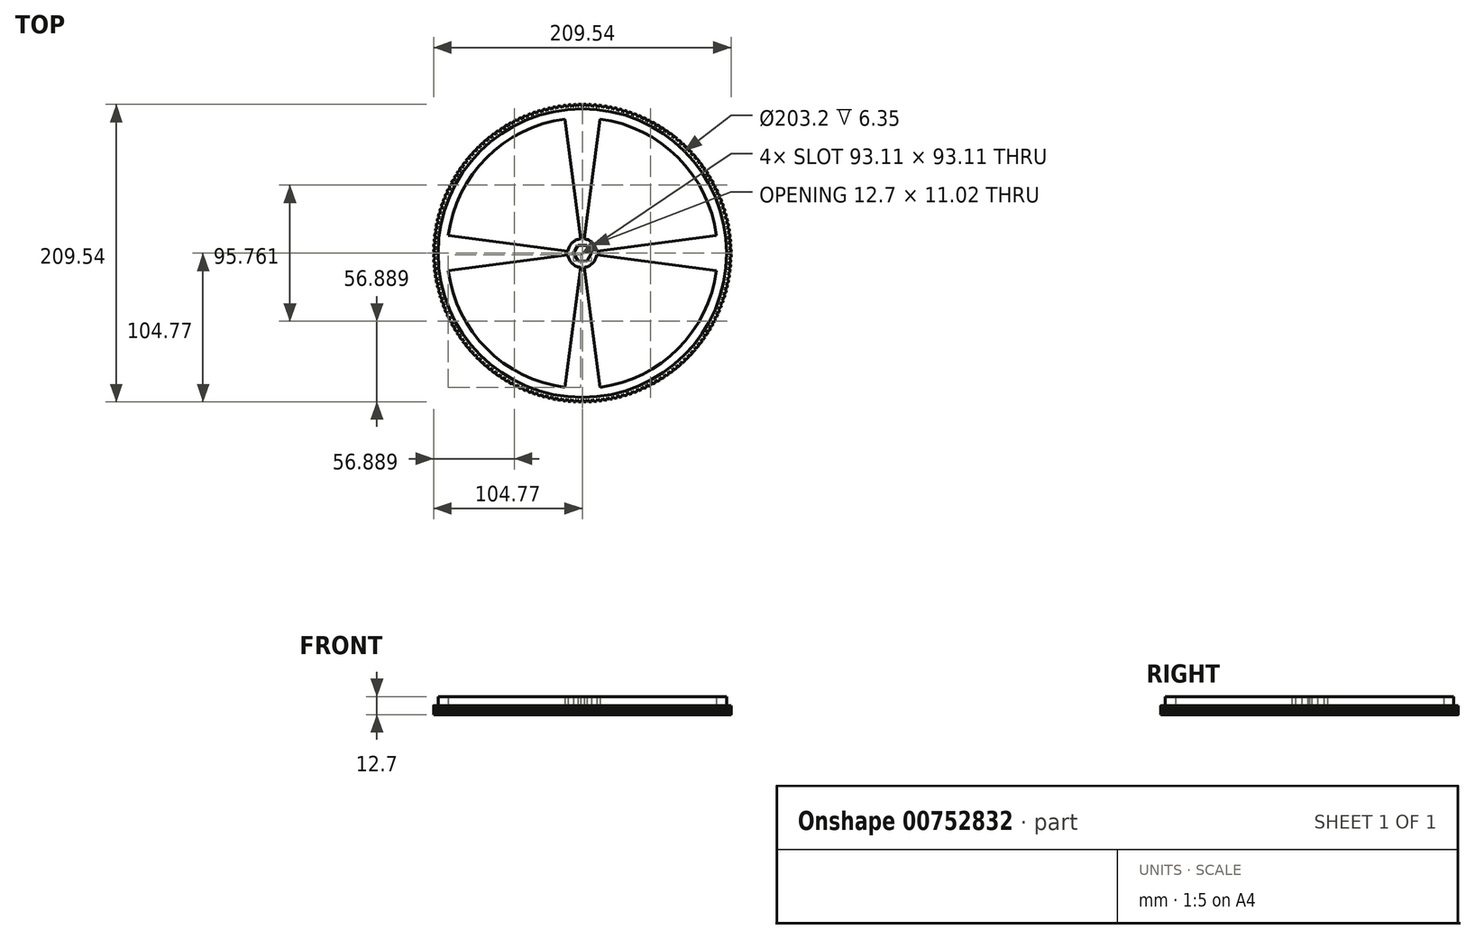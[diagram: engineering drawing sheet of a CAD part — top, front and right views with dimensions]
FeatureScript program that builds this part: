
annotation { "Feature Type Name" : "Feature", "Feature Type Description" : "" }
export const myFeature = defineFeature(function(context is Context, id is Id, definition is map)
    precondition{}
    {
        {
            var Q0;
            Q0=qCreatedBy(makeId("Top.planeOp"),FACE);
            var sketch = newSketch(context, id + "F0", { "sketchPlane" : qUnion([Q0])});
            skLineSegment(sketch, "E0.0", {"start": v(-3.15, 5.51) * mm, "end": v(3.2, 5.49) * mm});
            skLineSegment(sketch, "E0.1", {"start": v(3.2, 5.49) * mm, "end": v(6.35, -0.03) * mm});
            skLineSegment(sketch, "E0.2", {"start": v(6.35, -0.03) * mm, "end": v(3.15, -5.51) * mm});
            skLineSegment(sketch, "E0.3", {"start": v(3.15, -5.51) * mm, "end": v(-3.2, -5.49) * mm});
            skLineSegment(sketch, "E0.4", {"start": v(-3.2, -5.49) * mm, "end": v(-6.35, 0.03) * mm});
            skLineSegment(sketch, "E0.5", {"start": v(-6.35, 0.03) * mm, "end": v(-3.15, 5.51) * mm});
            skArc(sketch, "E1", {"start": v(-10.07, -1.33) * mm, "mid": v(-7.18, -7.18) * mm, "end": v(-1.33, -10.07) * mm});
            skCircle(sketch, "E2", {"center": v(0, 0) * mm, "radius": 101.6 * mm});
            skArc(sketch, "E3", {"start": v(94.44, 12.43) * mm, "mid": v(67.35, 67.35) * mm, "end": v(12.43, 94.44) * mm});
            skLineSegment(sketch, "E4", {"start": v(1.33, 10.07) * mm, "end": v(12.43, 94.44) * mm});
            skLineSegment(sketch, "E5", {"start": v(-1.33, 10.07) * mm, "end": v(-12.43, 94.44) * mm});
            skLineSegment(sketch, "E6.trimOffspring", {"start": v(-10.07, 1.33) * mm, "end": v(-94.44, 12.43) * mm});
            skLineSegment(sketch, "E7.trimOffspring", {"start": v(-10.07, -1.33) * mm, "end": v(-94.44, -12.43) * mm});
            skLineSegment(sketch, "E8.trimOffspring", {"start": v(-1.33, -10.07) * mm, "end": v(-12.43, -94.44) * mm});
            skLineSegment(sketch, "E9.trimOffspring", {"start": v(1.33, -10.07) * mm, "end": v(12.43, -94.44) * mm});
            skLineSegment(sketch, "E10.trimOffspring", {"start": v(10.07, -1.33) * mm, "end": v(94.44, -12.43) * mm});
            skLineSegment(sketch, "E11.trimOffspring", {"start": v(10.07, 1.33) * mm, "end": v(94.44, 12.43) * mm});
            skArc(sketch, "E12.trimOffspring", {"start": v(-12.43, 94.44) * mm, "mid": v(-67.35, 67.35) * mm, "end": v(-94.44, 12.43) * mm});
            skArc(sketch, "E13.trimOffspring", {"start": v(-94.44, -12.43) * mm, "mid": v(-67.35, -67.35) * mm, "end": v(-12.43, -94.44) * mm});
            skArc(sketch, "E14.trimOffspring", {"start": v(12.43, -94.44) * mm, "mid": v(67.35, -67.35) * mm, "end": v(94.44, -12.43) * mm});
            skArc(sketch, "E15.trimOffspring", {"start": v(-1.33, 10.07) * mm, "mid": v(-7.18, 7.18) * mm, "end": v(-10.07, 1.33) * mm});
            skArc(sketch, "E16.trimOffspring", {"start": v(10.07, 1.33) * mm, "mid": v(7.18, 7.18) * mm, "end": v(1.33, 10.07) * mm});
            skArc(sketch, "E17.trimOffspring", {"start": v(1.33, -10.07) * mm, "mid": v(7.18, -7.18) * mm, "end": v(10.07, -1.33) * mm});
            skSolve(sketch);
        }
        {
            var Q0;
            Q0 = qSketchRegion(id + "F0", true);
            extrude(context, id + "F1", {"entities" : qUnion([Q0]), "depth" : 6.35 * mm, "offsetDistance" : 25.4 * mm});
        }
        {
            var Q0;
            Q0=qCreatedBy(makeId("Top.planeOp"),FACE);
            var sketch = newSketch(context, id + "F2", { "sketchPlane" : qUnion([Q0])});
            skCircle(sketch, "E18", {"center": v(0, 0) * mm, "radius": 101.6 * mm});
            skCircle(sketch, "E19", {"center": v(0, 0) * mm, "radius": 104.78 * mm});
            skLineSegment(sketch, "E20", {"start": v(0, -103.19) * mm, "end": v(-0.91, -104.77) * mm});
            skLineSegment(sketch, "E21", {"start": v(0, -103.19) * mm, "end": v(0.91, -104.77) * mm});
            skLineSegment(sketch, "E22.1.0", {"start": v(3.6, -103.12) * mm, "end": v(4.57, -104.68) * mm});
            skLineSegment(sketch, "E22.1.1", {"start": v(3.6, -103.12) * mm, "end": v(2.74, -104.74) * mm});
            skLineSegment(sketch, "E22.2.0", {"start": v(7.2, -102.94) * mm, "end": v(8.22, -104.45) * mm});
            skLineSegment(sketch, "E22.2.1", {"start": v(7.2, -102.94) * mm, "end": v(6.4, -104.58) * mm});
            skLineSegment(sketch, "E22.3.0", {"start": v(10.79, -102.62) * mm, "end": v(11.86, -104.1) * mm});
            skLineSegment(sketch, "E22.3.1", {"start": v(10.79, -102.62) * mm, "end": v(10.04, -104.3) * mm});
            skLineSegment(sketch, "E22.4.0", {"start": v(14.36, -102.18) * mm, "end": v(15.49, -103.62) * mm});
            skLineSegment(sketch, "E22.4.1", {"start": v(14.36, -102.18) * mm, "end": v(13.68, -103.88) * mm});
            skLineSegment(sketch, "E22.5.0", {"start": v(17.92, -101.62) * mm, "end": v(19.1, -103.02) * mm});
            skLineSegment(sketch, "E22.5.1", {"start": v(17.92, -101.62) * mm, "end": v(17.3, -103.34) * mm});
            skLineSegment(sketch, "E22.6.0", {"start": v(21.45, -100.93) * mm, "end": v(22.68, -102.3) * mm});
            skLineSegment(sketch, "E22.6.1", {"start": v(21.45, -100.93) * mm, "end": v(20.89, -102.67) * mm});
            skLineSegment(sketch, "E22.7.0", {"start": v(24.96, -100.12) * mm, "end": v(26.23, -101.44) * mm});
            skLineSegment(sketch, "E22.7.1", {"start": v(24.96, -100.12) * mm, "end": v(24.46, -101.88) * mm});
            skLineSegment(sketch, "E22.8.0", {"start": v(28.44, -99.2) * mm, "end": v(29.76, -100.46) * mm});
            skLineSegment(sketch, "E22.8.1", {"start": v(28.44, -99.2) * mm, "end": v(28, -100.96) * mm});
            skLineSegment(sketch, "E22.9.0", {"start": v(31.89, -98.14) * mm, "end": v(33.25, -99.36) * mm});
            skLineSegment(sketch, "E22.9.1", {"start": v(31.89, -98.14) * mm, "end": v(31.5, -99.93) * mm});
            skLineSegment(sketch, "E22.10.0", {"start": v(35.3, -96.96) * mm, "end": v(36.7, -98.14) * mm});
            skLineSegment(sketch, "E22.10.1", {"start": v(35.3, -96.96) * mm, "end": v(34.97, -98.77) * mm});
            skLineSegment(sketch, "E22.11.0", {"start": v(38.65, -95.67) * mm, "end": v(40.1, -96.8) * mm});
            skLineSegment(sketch, "E22.11.1", {"start": v(38.65, -95.67) * mm, "end": v(38.4, -97.48) * mm});
            skLineSegment(sketch, "E22.12.0", {"start": v(41.97, -94.27) * mm, "end": v(43.45, -95.34) * mm});
            skLineSegment(sketch, "E22.12.1", {"start": v(41.97, -94.27) * mm, "end": v(41.78, -96.08) * mm});
            skLineSegment(sketch, "E22.13.0", {"start": v(45.23, -92.74) * mm, "end": v(46.75, -93.77) * mm});
            skLineSegment(sketch, "E22.13.1", {"start": v(45.23, -92.74) * mm, "end": v(45.1, -94.57) * mm});
            skLineSegment(sketch, "E22.14.0", {"start": v(48.44, -91.1) * mm, "end": v(50, -92.08) * mm});
            skLineSegment(sketch, "E22.14.1", {"start": v(48.44, -91.1) * mm, "end": v(48.38, -92.94) * mm});
            skLineSegment(sketch, "E22.15.0", {"start": v(51.6, -89.36) * mm, "end": v(53.18, -90.28) * mm});
            skLineSegment(sketch, "E22.15.1", {"start": v(51.6, -89.36) * mm, "end": v(51.6, -91.2) * mm});
            skLineSegment(sketch, "E22.16.0", {"start": v(54.68, -87.5) * mm, "end": v(56.3, -88.37) * mm});
            skLineSegment(sketch, "E22.16.1", {"start": v(54.68, -87.5) * mm, "end": v(54.74, -89.34) * mm});
            skLineSegment(sketch, "E22.17.0", {"start": v(57.7, -85.55) * mm, "end": v(59.35, -86.35) * mm});
            skLineSegment(sketch, "E22.17.1", {"start": v(57.7, -85.55) * mm, "end": v(57.83, -87.37) * mm});
            skLineSegment(sketch, "E22.18.0", {"start": v(60.65, -83.48) * mm, "end": v(62.32, -84.22) * mm});
            skLineSegment(sketch, "E22.18.1", {"start": v(60.65, -83.48) * mm, "end": v(60.84, -85.3) * mm});
            skLineSegment(sketch, "E22.19.0", {"start": v(63.53, -81.31) * mm, "end": v(65.22, -82) * mm});
            skLineSegment(sketch, "E22.19.1", {"start": v(63.53, -81.31) * mm, "end": v(63.78, -83.12) * mm});
            skLineSegment(sketch, "E22.20.0", {"start": v(66.33, -79.05) * mm, "end": v(68.05, -79.67) * mm});
            skLineSegment(sketch, "E22.20.1", {"start": v(66.33, -79.05) * mm, "end": v(66.65, -80.85) * mm});
            skLineSegment(sketch, "E22.21.0", {"start": v(69.05, -76.68) * mm, "end": v(70.78, -77.25) * mm});
            skLineSegment(sketch, "E22.21.1", {"start": v(69.05, -76.68) * mm, "end": v(69.43, -78.47) * mm});
            skLineSegment(sketch, "E22.22.0", {"start": v(71.68, -74.23) * mm, "end": v(73.44, -74.73) * mm});
            skLineSegment(sketch, "E22.22.1", {"start": v(71.68, -74.23) * mm, "end": v(72.12, -76) * mm});
            skLineSegment(sketch, "E22.23.0", {"start": v(74.23, -71.68) * mm, "end": v(76, -72.12) * mm});
            skLineSegment(sketch, "E22.23.1", {"start": v(74.23, -71.68) * mm, "end": v(74.73, -73.44) * mm});
            skLineSegment(sketch, "E22.24.0", {"start": v(76.68, -69.05) * mm, "end": v(78.47, -69.43) * mm});
            skLineSegment(sketch, "E22.24.1", {"start": v(76.68, -69.05) * mm, "end": v(77.25, -70.78) * mm});
            skLineSegment(sketch, "E22.25.0", {"start": v(79.05, -66.33) * mm, "end": v(80.85, -66.65) * mm});
            skLineSegment(sketch, "E22.25.1", {"start": v(79.05, -66.33) * mm, "end": v(79.67, -68.05) * mm});
            skLineSegment(sketch, "E22.26.0", {"start": v(81.31, -63.53) * mm, "end": v(83.12, -63.78) * mm});
            skLineSegment(sketch, "E22.26.1", {"start": v(81.31, -63.53) * mm, "end": v(82, -65.22) * mm});
            skLineSegment(sketch, "E22.27.0", {"start": v(83.48, -60.65) * mm, "end": v(85.3, -60.84) * mm});
            skLineSegment(sketch, "E22.27.1", {"start": v(83.48, -60.65) * mm, "end": v(84.22, -62.32) * mm});
            skLineSegment(sketch, "E22.28.0", {"start": v(85.55, -57.7) * mm, "end": v(87.37, -57.83) * mm});
            skLineSegment(sketch, "E22.28.1", {"start": v(85.55, -57.7) * mm, "end": v(86.35, -59.35) * mm});
            skLineSegment(sketch, "E22.29.0", {"start": v(87.5, -54.68) * mm, "end": v(89.34, -54.74) * mm});
            skLineSegment(sketch, "E22.29.1", {"start": v(87.5, -54.68) * mm, "end": v(88.37, -56.3) * mm});
            skLineSegment(sketch, "E22.30.0", {"start": v(89.36, -51.6) * mm, "end": v(91.2, -51.6) * mm});
            skLineSegment(sketch, "E22.30.1", {"start": v(89.36, -51.6) * mm, "end": v(90.28, -53.18) * mm});
            skLineSegment(sketch, "E22.31.0", {"start": v(91.1, -48.44) * mm, "end": v(92.94, -48.38) * mm});
            skLineSegment(sketch, "E22.31.1", {"start": v(91.1, -48.44) * mm, "end": v(92.08, -50) * mm});
            skLineSegment(sketch, "E22.32.0", {"start": v(92.74, -45.23) * mm, "end": v(94.57, -45.1) * mm});
            skLineSegment(sketch, "E22.32.1", {"start": v(92.74, -45.23) * mm, "end": v(93.77, -46.75) * mm});
            skLineSegment(sketch, "E22.33.0", {"start": v(94.27, -41.97) * mm, "end": v(96.08, -41.78) * mm});
            skLineSegment(sketch, "E22.33.1", {"start": v(94.27, -41.97) * mm, "end": v(95.34, -43.45) * mm});
            skLineSegment(sketch, "E22.34.0", {"start": v(95.67, -38.65) * mm, "end": v(97.48, -38.4) * mm});
            skLineSegment(sketch, "E22.34.1", {"start": v(95.67, -38.65) * mm, "end": v(96.8, -40.1) * mm});
            skLineSegment(sketch, "E22.35.0", {"start": v(96.96, -35.3) * mm, "end": v(98.77, -34.97) * mm});
            skLineSegment(sketch, "E22.35.1", {"start": v(96.96, -35.3) * mm, "end": v(98.14, -36.7) * mm});
            skLineSegment(sketch, "E22.36.0", {"start": v(98.14, -31.89) * mm, "end": v(99.93, -31.5) * mm});
            skLineSegment(sketch, "E22.36.1", {"start": v(98.14, -31.89) * mm, "end": v(99.36, -33.25) * mm});
            skLineSegment(sketch, "E22.37.0", {"start": v(99.2, -28.44) * mm, "end": v(100.96, -28) * mm});
            skLineSegment(sketch, "E22.37.1", {"start": v(99.2, -28.44) * mm, "end": v(100.46, -29.76) * mm});
            skLineSegment(sketch, "E22.38.0", {"start": v(100.12, -24.96) * mm, "end": v(101.88, -24.46) * mm});
            skLineSegment(sketch, "E22.38.1", {"start": v(100.12, -24.96) * mm, "end": v(101.44, -26.23) * mm});
            skLineSegment(sketch, "E22.39.0", {"start": v(100.93, -21.45) * mm, "end": v(102.67, -20.89) * mm});
            skLineSegment(sketch, "E22.39.1", {"start": v(100.93, -21.45) * mm, "end": v(102.3, -22.68) * mm});
            skLineSegment(sketch, "E22.40.0", {"start": v(101.62, -17.92) * mm, "end": v(103.34, -17.3) * mm});
            skLineSegment(sketch, "E22.40.1", {"start": v(101.62, -17.92) * mm, "end": v(103.02, -19.1) * mm});
            skLineSegment(sketch, "E22.41.0", {"start": v(102.18, -14.36) * mm, "end": v(103.88, -13.68) * mm});
            skLineSegment(sketch, "E22.41.1", {"start": v(102.18, -14.36) * mm, "end": v(103.62, -15.49) * mm});
            skLineSegment(sketch, "E22.42.0", {"start": v(102.62, -10.79) * mm, "end": v(104.3, -10.04) * mm});
            skLineSegment(sketch, "E22.42.1", {"start": v(102.62, -10.79) * mm, "end": v(104.1, -11.86) * mm});
            skLineSegment(sketch, "E22.43.0", {"start": v(102.94, -7.2) * mm, "end": v(104.58, -6.4) * mm});
            skLineSegment(sketch, "E22.43.1", {"start": v(102.94, -7.2) * mm, "end": v(104.45, -8.22) * mm});
            skLineSegment(sketch, "E22.44.0", {"start": v(103.12, -3.6) * mm, "end": v(104.74, -2.74) * mm});
            skLineSegment(sketch, "E22.44.1", {"start": v(103.12, -3.6) * mm, "end": v(104.68, -4.57) * mm});
            skLineSegment(sketch, "E22.45.0", {"start": v(103.19, 0) * mm, "end": v(104.77, 0.91) * mm});
            skLineSegment(sketch, "E22.45.1", {"start": v(103.19, 0) * mm, "end": v(104.77, -0.91) * mm});
            skLineSegment(sketch, "E22.46.0", {"start": v(103.12, 3.6) * mm, "end": v(104.68, 4.57) * mm});
            skLineSegment(sketch, "E22.46.1", {"start": v(103.12, 3.6) * mm, "end": v(104.74, 2.74) * mm});
            skLineSegment(sketch, "E22.47.0", {"start": v(102.94, 7.2) * mm, "end": v(104.45, 8.22) * mm});
            skLineSegment(sketch, "E22.47.1", {"start": v(102.94, 7.2) * mm, "end": v(104.58, 6.4) * mm});
            skLineSegment(sketch, "E22.48.0", {"start": v(102.62, 10.79) * mm, "end": v(104.1, 11.86) * mm});
            skLineSegment(sketch, "E22.48.1", {"start": v(102.62, 10.79) * mm, "end": v(104.3, 10.04) * mm});
            skLineSegment(sketch, "E22.49.0", {"start": v(102.18, 14.36) * mm, "end": v(103.62, 15.49) * mm});
            skLineSegment(sketch, "E22.49.1", {"start": v(102.18, 14.36) * mm, "end": v(103.88, 13.68) * mm});
            skLineSegment(sketch, "E22.50.0", {"start": v(101.62, 17.92) * mm, "end": v(103.02, 19.1) * mm});
            skLineSegment(sketch, "E22.50.1", {"start": v(101.62, 17.92) * mm, "end": v(103.34, 17.3) * mm});
            skLineSegment(sketch, "E22.51.0", {"start": v(100.93, 21.45) * mm, "end": v(102.3, 22.68) * mm});
            skLineSegment(sketch, "E22.51.1", {"start": v(100.93, 21.45) * mm, "end": v(102.67, 20.89) * mm});
            skLineSegment(sketch, "E22.52.0", {"start": v(100.12, 24.96) * mm, "end": v(101.44, 26.23) * mm});
            skLineSegment(sketch, "E22.52.1", {"start": v(100.12, 24.96) * mm, "end": v(101.88, 24.46) * mm});
            skLineSegment(sketch, "E22.53.0", {"start": v(99.2, 28.44) * mm, "end": v(100.46, 29.76) * mm});
            skLineSegment(sketch, "E22.53.1", {"start": v(99.2, 28.44) * mm, "end": v(100.96, 28) * mm});
            skLineSegment(sketch, "E22.54.0", {"start": v(98.14, 31.89) * mm, "end": v(99.36, 33.25) * mm});
            skLineSegment(sketch, "E22.54.1", {"start": v(98.14, 31.89) * mm, "end": v(99.93, 31.5) * mm});
            skLineSegment(sketch, "E22.55.0", {"start": v(96.96, 35.3) * mm, "end": v(98.14, 36.7) * mm});
            skLineSegment(sketch, "E22.55.1", {"start": v(96.96, 35.3) * mm, "end": v(98.77, 34.97) * mm});
            skLineSegment(sketch, "E22.56.0", {"start": v(95.67, 38.65) * mm, "end": v(96.8, 40.1) * mm});
            skLineSegment(sketch, "E22.56.1", {"start": v(95.67, 38.65) * mm, "end": v(97.48, 38.4) * mm});
            skLineSegment(sketch, "E22.57.0", {"start": v(94.27, 41.97) * mm, "end": v(95.34, 43.45) * mm});
            skLineSegment(sketch, "E22.57.1", {"start": v(94.27, 41.97) * mm, "end": v(96.08, 41.78) * mm});
            skLineSegment(sketch, "E22.58.0", {"start": v(92.74, 45.23) * mm, "end": v(93.77, 46.75) * mm});
            skLineSegment(sketch, "E22.58.1", {"start": v(92.74, 45.23) * mm, "end": v(94.57, 45.1) * mm});
            skLineSegment(sketch, "E22.59.0", {"start": v(91.1, 48.44) * mm, "end": v(92.08, 50) * mm});
            skLineSegment(sketch, "E22.59.1", {"start": v(91.1, 48.44) * mm, "end": v(92.94, 48.38) * mm});
            skLineSegment(sketch, "E22.60.0", {"start": v(89.36, 51.6) * mm, "end": v(90.28, 53.18) * mm});
            skLineSegment(sketch, "E22.60.1", {"start": v(89.36, 51.6) * mm, "end": v(91.2, 51.6) * mm});
            skLineSegment(sketch, "E22.61.0", {"start": v(87.5, 54.68) * mm, "end": v(88.37, 56.3) * mm});
            skLineSegment(sketch, "E22.61.1", {"start": v(87.5, 54.68) * mm, "end": v(89.34, 54.74) * mm});
            skLineSegment(sketch, "E22.62.0", {"start": v(85.55, 57.7) * mm, "end": v(86.35, 59.35) * mm});
            skLineSegment(sketch, "E22.62.1", {"start": v(85.55, 57.7) * mm, "end": v(87.37, 57.83) * mm});
            skLineSegment(sketch, "E22.63.0", {"start": v(83.48, 60.65) * mm, "end": v(84.22, 62.32) * mm});
            skLineSegment(sketch, "E22.63.1", {"start": v(83.48, 60.65) * mm, "end": v(85.3, 60.84) * mm});
            skLineSegment(sketch, "E22.64.0", {"start": v(81.31, 63.53) * mm, "end": v(82, 65.22) * mm});
            skLineSegment(sketch, "E22.64.1", {"start": v(81.31, 63.53) * mm, "end": v(83.12, 63.78) * mm});
            skLineSegment(sketch, "E22.65.0", {"start": v(79.05, 66.33) * mm, "end": v(79.67, 68.05) * mm});
            skLineSegment(sketch, "E22.65.1", {"start": v(79.05, 66.33) * mm, "end": v(80.85, 66.65) * mm});
            skLineSegment(sketch, "E22.66.0", {"start": v(76.68, 69.05) * mm, "end": v(77.25, 70.78) * mm});
            skLineSegment(sketch, "E22.66.1", {"start": v(76.68, 69.05) * mm, "end": v(78.47, 69.43) * mm});
            skLineSegment(sketch, "E22.67.0", {"start": v(74.23, 71.68) * mm, "end": v(74.73, 73.44) * mm});
            skLineSegment(sketch, "E22.67.1", {"start": v(74.23, 71.68) * mm, "end": v(76, 72.12) * mm});
            skLineSegment(sketch, "E22.68.0", {"start": v(71.68, 74.23) * mm, "end": v(72.12, 76) * mm});
            skLineSegment(sketch, "E22.68.1", {"start": v(71.68, 74.23) * mm, "end": v(73.44, 74.73) * mm});
            skLineSegment(sketch, "E22.69.0", {"start": v(69.05, 76.68) * mm, "end": v(69.43, 78.47) * mm});
            skLineSegment(sketch, "E22.69.1", {"start": v(69.05, 76.68) * mm, "end": v(70.78, 77.25) * mm});
            skLineSegment(sketch, "E22.70.0", {"start": v(66.33, 79.05) * mm, "end": v(66.65, 80.85) * mm});
            skLineSegment(sketch, "E22.70.1", {"start": v(66.33, 79.05) * mm, "end": v(68.05, 79.67) * mm});
            skLineSegment(sketch, "E22.71.0", {"start": v(63.53, 81.31) * mm, "end": v(63.78, 83.12) * mm});
            skLineSegment(sketch, "E22.71.1", {"start": v(63.53, 81.31) * mm, "end": v(65.22, 82) * mm});
            skLineSegment(sketch, "E22.72.0", {"start": v(60.65, 83.48) * mm, "end": v(60.84, 85.3) * mm});
            skLineSegment(sketch, "E22.72.1", {"start": v(60.65, 83.48) * mm, "end": v(62.32, 84.22) * mm});
            skLineSegment(sketch, "E22.73.0", {"start": v(57.7, 85.55) * mm, "end": v(57.83, 87.37) * mm});
            skLineSegment(sketch, "E22.73.1", {"start": v(57.7, 85.55) * mm, "end": v(59.35, 86.35) * mm});
            skLineSegment(sketch, "E22.74.0", {"start": v(54.68, 87.5) * mm, "end": v(54.74, 89.34) * mm});
            skLineSegment(sketch, "E22.74.1", {"start": v(54.68, 87.5) * mm, "end": v(56.3, 88.37) * mm});
            skLineSegment(sketch, "E22.75.0", {"start": v(51.6, 89.36) * mm, "end": v(51.6, 91.2) * mm});
            skLineSegment(sketch, "E22.75.1", {"start": v(51.6, 89.36) * mm, "end": v(53.18, 90.28) * mm});
            skLineSegment(sketch, "E22.76.0", {"start": v(48.44, 91.1) * mm, "end": v(48.38, 92.94) * mm});
            skLineSegment(sketch, "E22.76.1", {"start": v(48.44, 91.1) * mm, "end": v(50, 92.08) * mm});
            skLineSegment(sketch, "E22.77.0", {"start": v(45.23, 92.74) * mm, "end": v(45.1, 94.57) * mm});
            skLineSegment(sketch, "E22.77.1", {"start": v(45.23, 92.74) * mm, "end": v(46.75, 93.77) * mm});
            skLineSegment(sketch, "E22.78.0", {"start": v(41.97, 94.27) * mm, "end": v(41.78, 96.08) * mm});
            skLineSegment(sketch, "E22.78.1", {"start": v(41.97, 94.27) * mm, "end": v(43.45, 95.34) * mm});
            skLineSegment(sketch, "E22.79.0", {"start": v(38.65, 95.67) * mm, "end": v(38.4, 97.48) * mm});
            skLineSegment(sketch, "E22.79.1", {"start": v(38.65, 95.67) * mm, "end": v(40.1, 96.8) * mm});
            skLineSegment(sketch, "E22.80.0", {"start": v(35.3, 96.96) * mm, "end": v(34.97, 98.77) * mm});
            skLineSegment(sketch, "E22.80.1", {"start": v(35.3, 96.96) * mm, "end": v(36.7, 98.14) * mm});
            skLineSegment(sketch, "E22.81.0", {"start": v(31.89, 98.14) * mm, "end": v(31.5, 99.93) * mm});
            skLineSegment(sketch, "E22.81.1", {"start": v(31.89, 98.14) * mm, "end": v(33.25, 99.36) * mm});
            skLineSegment(sketch, "E22.82.0", {"start": v(28.44, 99.2) * mm, "end": v(28, 100.96) * mm});
            skLineSegment(sketch, "E22.82.1", {"start": v(28.44, 99.2) * mm, "end": v(29.76, 100.46) * mm});
            skLineSegment(sketch, "E22.83.0", {"start": v(24.96, 100.12) * mm, "end": v(24.46, 101.88) * mm});
            skLineSegment(sketch, "E22.83.1", {"start": v(24.96, 100.12) * mm, "end": v(26.23, 101.44) * mm});
            skLineSegment(sketch, "E22.84.0", {"start": v(21.45, 100.93) * mm, "end": v(20.89, 102.67) * mm});
            skLineSegment(sketch, "E22.84.1", {"start": v(21.45, 100.93) * mm, "end": v(22.68, 102.3) * mm});
            skLineSegment(sketch, "E22.85.0", {"start": v(17.92, 101.62) * mm, "end": v(17.3, 103.34) * mm});
            skLineSegment(sketch, "E22.85.1", {"start": v(17.92, 101.62) * mm, "end": v(19.1, 103.02) * mm});
            skLineSegment(sketch, "E22.86.0", {"start": v(14.36, 102.18) * mm, "end": v(13.68, 103.88) * mm});
            skLineSegment(sketch, "E22.86.1", {"start": v(14.36, 102.18) * mm, "end": v(15.49, 103.62) * mm});
            skLineSegment(sketch, "E22.87.0", {"start": v(10.79, 102.62) * mm, "end": v(10.04, 104.3) * mm});
            skLineSegment(sketch, "E22.87.1", {"start": v(10.79, 102.62) * mm, "end": v(11.86, 104.1) * mm});
            skLineSegment(sketch, "E22.88.0", {"start": v(7.2, 102.94) * mm, "end": v(6.4, 104.58) * mm});
            skLineSegment(sketch, "E22.88.1", {"start": v(7.2, 102.94) * mm, "end": v(8.22, 104.45) * mm});
            skLineSegment(sketch, "E22.89.0", {"start": v(3.6, 103.12) * mm, "end": v(2.74, 104.74) * mm});
            skLineSegment(sketch, "E22.89.1", {"start": v(3.6, 103.12) * mm, "end": v(4.57, 104.68) * mm});
            skLineSegment(sketch, "E22.90.0", {"start": v(0, 103.19) * mm, "end": v(-0.91, 104.77) * mm});
            skLineSegment(sketch, "E22.90.1", {"start": v(0, 103.19) * mm, "end": v(0.91, 104.77) * mm});
            skLineSegment(sketch, "E22.91.0", {"start": v(-3.6, 103.12) * mm, "end": v(-4.57, 104.68) * mm});
            skLineSegment(sketch, "E22.91.1", {"start": v(-3.6, 103.12) * mm, "end": v(-2.74, 104.74) * mm});
            skLineSegment(sketch, "E22.92.0", {"start": v(-7.2, 102.94) * mm, "end": v(-8.22, 104.45) * mm});
            skLineSegment(sketch, "E22.92.1", {"start": v(-7.2, 102.94) * mm, "end": v(-6.4, 104.58) * mm});
            skLineSegment(sketch, "E22.93.0", {"start": v(-10.79, 102.62) * mm, "end": v(-11.86, 104.1) * mm});
            skLineSegment(sketch, "E22.93.1", {"start": v(-10.79, 102.62) * mm, "end": v(-10.04, 104.3) * mm});
            skLineSegment(sketch, "E22.94.0", {"start": v(-14.36, 102.18) * mm, "end": v(-15.49, 103.62) * mm});
            skLineSegment(sketch, "E22.94.1", {"start": v(-14.36, 102.18) * mm, "end": v(-13.68, 103.88) * mm});
            skLineSegment(sketch, "E22.95.0", {"start": v(-17.92, 101.62) * mm, "end": v(-19.1, 103.02) * mm});
            skLineSegment(sketch, "E22.95.1", {"start": v(-17.92, 101.62) * mm, "end": v(-17.3, 103.34) * mm});
            skLineSegment(sketch, "E22.96.0", {"start": v(-21.45, 100.93) * mm, "end": v(-22.68, 102.3) * mm});
            skLineSegment(sketch, "E22.96.1", {"start": v(-21.45, 100.93) * mm, "end": v(-20.89, 102.67) * mm});
            skLineSegment(sketch, "E22.97.0", {"start": v(-24.96, 100.12) * mm, "end": v(-26.23, 101.44) * mm});
            skLineSegment(sketch, "E22.97.1", {"start": v(-24.96, 100.12) * mm, "end": v(-24.46, 101.88) * mm});
            skLineSegment(sketch, "E22.98.0", {"start": v(-28.44, 99.2) * mm, "end": v(-29.76, 100.46) * mm});
            skLineSegment(sketch, "E22.98.1", {"start": v(-28.44, 99.2) * mm, "end": v(-28, 100.96) * mm});
            skLineSegment(sketch, "E22.99.0", {"start": v(-31.89, 98.14) * mm, "end": v(-33.25, 99.36) * mm});
            skLineSegment(sketch, "E22.99.1", {"start": v(-31.89, 98.14) * mm, "end": v(-31.5, 99.93) * mm});
            skLineSegment(sketch, "E22.100.0", {"start": v(-35.3, 96.96) * mm, "end": v(-36.7, 98.14) * mm});
            skLineSegment(sketch, "E22.100.1", {"start": v(-35.3, 96.96) * mm, "end": v(-34.97, 98.77) * mm});
            skLineSegment(sketch, "E22.101.0", {"start": v(-38.65, 95.67) * mm, "end": v(-40.1, 96.8) * mm});
            skLineSegment(sketch, "E22.101.1", {"start": v(-38.65, 95.67) * mm, "end": v(-38.4, 97.48) * mm});
            skLineSegment(sketch, "E22.102.0", {"start": v(-41.97, 94.27) * mm, "end": v(-43.45, 95.34) * mm});
            skLineSegment(sketch, "E22.102.1", {"start": v(-41.97, 94.27) * mm, "end": v(-41.78, 96.08) * mm});
            skLineSegment(sketch, "E22.103.0", {"start": v(-45.23, 92.74) * mm, "end": v(-46.75, 93.77) * mm});
            skLineSegment(sketch, "E22.103.1", {"start": v(-45.23, 92.74) * mm, "end": v(-45.1, 94.57) * mm});
            skLineSegment(sketch, "E22.104.0", {"start": v(-48.44, 91.1) * mm, "end": v(-50, 92.08) * mm});
            skLineSegment(sketch, "E22.104.1", {"start": v(-48.44, 91.1) * mm, "end": v(-48.38, 92.94) * mm});
            skLineSegment(sketch, "E22.105.0", {"start": v(-51.6, 89.36) * mm, "end": v(-53.18, 90.28) * mm});
            skLineSegment(sketch, "E22.105.1", {"start": v(-51.6, 89.36) * mm, "end": v(-51.6, 91.2) * mm});
            skLineSegment(sketch, "E22.106.0", {"start": v(-54.68, 87.5) * mm, "end": v(-56.3, 88.37) * mm});
            skLineSegment(sketch, "E22.106.1", {"start": v(-54.68, 87.5) * mm, "end": v(-54.74, 89.34) * mm});
            skLineSegment(sketch, "E22.107.0", {"start": v(-57.7, 85.55) * mm, "end": v(-59.35, 86.35) * mm});
            skLineSegment(sketch, "E22.107.1", {"start": v(-57.7, 85.55) * mm, "end": v(-57.83, 87.37) * mm});
            skLineSegment(sketch, "E22.108.0", {"start": v(-60.65, 83.48) * mm, "end": v(-62.32, 84.22) * mm});
            skLineSegment(sketch, "E22.108.1", {"start": v(-60.65, 83.48) * mm, "end": v(-60.84, 85.3) * mm});
            skLineSegment(sketch, "E22.109.0", {"start": v(-63.53, 81.31) * mm, "end": v(-65.22, 82) * mm});
            skLineSegment(sketch, "E22.109.1", {"start": v(-63.53, 81.31) * mm, "end": v(-63.78, 83.12) * mm});
            skLineSegment(sketch, "E22.110.0", {"start": v(-66.33, 79.05) * mm, "end": v(-68.05, 79.67) * mm});
            skLineSegment(sketch, "E22.110.1", {"start": v(-66.33, 79.05) * mm, "end": v(-66.65, 80.85) * mm});
            skLineSegment(sketch, "E22.111.0", {"start": v(-69.05, 76.68) * mm, "end": v(-70.78, 77.25) * mm});
            skLineSegment(sketch, "E22.111.1", {"start": v(-69.05, 76.68) * mm, "end": v(-69.43, 78.47) * mm});
            skLineSegment(sketch, "E22.112.0", {"start": v(-71.68, 74.23) * mm, "end": v(-73.44, 74.73) * mm});
            skLineSegment(sketch, "E22.112.1", {"start": v(-71.68, 74.23) * mm, "end": v(-72.12, 76) * mm});
            skLineSegment(sketch, "E22.113.0", {"start": v(-74.23, 71.68) * mm, "end": v(-76, 72.12) * mm});
            skLineSegment(sketch, "E22.113.1", {"start": v(-74.23, 71.68) * mm, "end": v(-74.73, 73.44) * mm});
            skLineSegment(sketch, "E22.114.0", {"start": v(-76.68, 69.05) * mm, "end": v(-78.47, 69.43) * mm});
            skLineSegment(sketch, "E22.114.1", {"start": v(-76.68, 69.05) * mm, "end": v(-77.25, 70.78) * mm});
            skLineSegment(sketch, "E22.115.0", {"start": v(-79.05, 66.33) * mm, "end": v(-80.85, 66.65) * mm});
            skLineSegment(sketch, "E22.115.1", {"start": v(-79.05, 66.33) * mm, "end": v(-79.67, 68.05) * mm});
            skLineSegment(sketch, "E22.116.0", {"start": v(-81.31, 63.53) * mm, "end": v(-83.12, 63.78) * mm});
            skLineSegment(sketch, "E22.116.1", {"start": v(-81.31, 63.53) * mm, "end": v(-82, 65.22) * mm});
            skLineSegment(sketch, "E22.117.0", {"start": v(-83.48, 60.65) * mm, "end": v(-85.3, 60.84) * mm});
            skLineSegment(sketch, "E22.117.1", {"start": v(-83.48, 60.65) * mm, "end": v(-84.22, 62.32) * mm});
            skLineSegment(sketch, "E22.118.0", {"start": v(-85.55, 57.7) * mm, "end": v(-87.37, 57.83) * mm});
            skLineSegment(sketch, "E22.118.1", {"start": v(-85.55, 57.7) * mm, "end": v(-86.35, 59.35) * mm});
            skLineSegment(sketch, "E22.119.0", {"start": v(-87.5, 54.68) * mm, "end": v(-89.34, 54.74) * mm});
            skLineSegment(sketch, "E22.119.1", {"start": v(-87.5, 54.68) * mm, "end": v(-88.37, 56.3) * mm});
            skLineSegment(sketch, "E22.120.0", {"start": v(-89.36, 51.6) * mm, "end": v(-91.2, 51.6) * mm});
            skLineSegment(sketch, "E22.120.1", {"start": v(-89.36, 51.6) * mm, "end": v(-90.28, 53.18) * mm});
            skLineSegment(sketch, "E22.121.0", {"start": v(-91.1, 48.44) * mm, "end": v(-92.94, 48.38) * mm});
            skLineSegment(sketch, "E22.121.1", {"start": v(-91.1, 48.44) * mm, "end": v(-92.08, 50) * mm});
            skLineSegment(sketch, "E22.122.0", {"start": v(-92.74, 45.23) * mm, "end": v(-94.57, 45.1) * mm});
            skLineSegment(sketch, "E22.122.1", {"start": v(-92.74, 45.23) * mm, "end": v(-93.77, 46.75) * mm});
            skLineSegment(sketch, "E22.123.0", {"start": v(-94.27, 41.97) * mm, "end": v(-96.08, 41.78) * mm});
            skLineSegment(sketch, "E22.123.1", {"start": v(-94.27, 41.97) * mm, "end": v(-95.34, 43.45) * mm});
            skLineSegment(sketch, "E22.124.0", {"start": v(-95.67, 38.65) * mm, "end": v(-97.48, 38.4) * mm});
            skLineSegment(sketch, "E22.124.1", {"start": v(-95.67, 38.65) * mm, "end": v(-96.8, 40.1) * mm});
            skLineSegment(sketch, "E22.125.0", {"start": v(-96.96, 35.3) * mm, "end": v(-98.77, 34.97) * mm});
            skLineSegment(sketch, "E22.125.1", {"start": v(-96.96, 35.3) * mm, "end": v(-98.14, 36.7) * mm});
            skLineSegment(sketch, "E22.126.0", {"start": v(-98.14, 31.89) * mm, "end": v(-99.93, 31.5) * mm});
            skLineSegment(sketch, "E22.126.1", {"start": v(-98.14, 31.89) * mm, "end": v(-99.36, 33.25) * mm});
            skLineSegment(sketch, "E22.127.0", {"start": v(-99.2, 28.44) * mm, "end": v(-100.96, 28) * mm});
            skLineSegment(sketch, "E22.127.1", {"start": v(-99.2, 28.44) * mm, "end": v(-100.46, 29.76) * mm});
            skLineSegment(sketch, "E22.128.0", {"start": v(-100.12, 24.96) * mm, "end": v(-101.88, 24.46) * mm});
            skLineSegment(sketch, "E22.128.1", {"start": v(-100.12, 24.96) * mm, "end": v(-101.44, 26.23) * mm});
            skLineSegment(sketch, "E22.129.0", {"start": v(-100.93, 21.45) * mm, "end": v(-102.67, 20.89) * mm});
            skLineSegment(sketch, "E22.129.1", {"start": v(-100.93, 21.45) * mm, "end": v(-102.3, 22.68) * mm});
            skLineSegment(sketch, "E22.130.0", {"start": v(-101.62, 17.92) * mm, "end": v(-103.34, 17.3) * mm});
            skLineSegment(sketch, "E22.130.1", {"start": v(-101.62, 17.92) * mm, "end": v(-103.02, 19.1) * mm});
            skLineSegment(sketch, "E22.131.0", {"start": v(-102.18, 14.36) * mm, "end": v(-103.88, 13.68) * mm});
            skLineSegment(sketch, "E22.131.1", {"start": v(-102.18, 14.36) * mm, "end": v(-103.62, 15.49) * mm});
            skLineSegment(sketch, "E22.132.0", {"start": v(-102.62, 10.79) * mm, "end": v(-104.3, 10.04) * mm});
            skLineSegment(sketch, "E22.132.1", {"start": v(-102.62, 10.79) * mm, "end": v(-104.1, 11.86) * mm});
            skLineSegment(sketch, "E22.133.0", {"start": v(-102.94, 7.2) * mm, "end": v(-104.58, 6.4) * mm});
            skLineSegment(sketch, "E22.133.1", {"start": v(-102.94, 7.2) * mm, "end": v(-104.45, 8.22) * mm});
            skLineSegment(sketch, "E22.134.0", {"start": v(-103.12, 3.6) * mm, "end": v(-104.74, 2.74) * mm});
            skLineSegment(sketch, "E22.134.1", {"start": v(-103.12, 3.6) * mm, "end": v(-104.68, 4.57) * mm});
            skLineSegment(sketch, "E22.135.0", {"start": v(-103.19, 0) * mm, "end": v(-104.77, -0.91) * mm});
            skLineSegment(sketch, "E22.135.1", {"start": v(-103.19, 0) * mm, "end": v(-104.77, 0.91) * mm});
            skLineSegment(sketch, "E22.136.0", {"start": v(-103.12, -3.6) * mm, "end": v(-104.68, -4.57) * mm});
            skLineSegment(sketch, "E22.136.1", {"start": v(-103.12, -3.6) * mm, "end": v(-104.74, -2.74) * mm});
            skLineSegment(sketch, "E22.137.0", {"start": v(-102.94, -7.2) * mm, "end": v(-104.45, -8.22) * mm});
            skLineSegment(sketch, "E22.137.1", {"start": v(-102.94, -7.2) * mm, "end": v(-104.58, -6.4) * mm});
            skLineSegment(sketch, "E22.138.0", {"start": v(-102.62, -10.79) * mm, "end": v(-104.1, -11.86) * mm});
            skLineSegment(sketch, "E22.138.1", {"start": v(-102.62, -10.79) * mm, "end": v(-104.3, -10.04) * mm});
            skLineSegment(sketch, "E22.139.0", {"start": v(-102.18, -14.36) * mm, "end": v(-103.62, -15.49) * mm});
            skLineSegment(sketch, "E22.139.1", {"start": v(-102.18, -14.36) * mm, "end": v(-103.88, -13.68) * mm});
            skLineSegment(sketch, "E22.140.0", {"start": v(-101.62, -17.92) * mm, "end": v(-103.02, -19.1) * mm});
            skLineSegment(sketch, "E22.140.1", {"start": v(-101.62, -17.92) * mm, "end": v(-103.34, -17.3) * mm});
            skLineSegment(sketch, "E22.141.0", {"start": v(-100.93, -21.45) * mm, "end": v(-102.3, -22.68) * mm});
            skLineSegment(sketch, "E22.141.1", {"start": v(-100.93, -21.45) * mm, "end": v(-102.67, -20.89) * mm});
            skLineSegment(sketch, "E22.142.0", {"start": v(-100.12, -24.96) * mm, "end": v(-101.44, -26.23) * mm});
            skLineSegment(sketch, "E22.142.1", {"start": v(-100.12, -24.96) * mm, "end": v(-101.88, -24.46) * mm});
            skLineSegment(sketch, "E22.143.0", {"start": v(-99.2, -28.44) * mm, "end": v(-100.46, -29.76) * mm});
            skLineSegment(sketch, "E22.143.1", {"start": v(-99.2, -28.44) * mm, "end": v(-100.96, -28) * mm});
            skLineSegment(sketch, "E22.144.0", {"start": v(-98.14, -31.89) * mm, "end": v(-99.36, -33.25) * mm});
            skLineSegment(sketch, "E22.144.1", {"start": v(-98.14, -31.89) * mm, "end": v(-99.93, -31.5) * mm});
            skLineSegment(sketch, "E22.145.0", {"start": v(-96.96, -35.3) * mm, "end": v(-98.14, -36.7) * mm});
            skLineSegment(sketch, "E22.145.1", {"start": v(-96.96, -35.3) * mm, "end": v(-98.77, -34.97) * mm});
            skLineSegment(sketch, "E22.146.0", {"start": v(-95.67, -38.65) * mm, "end": v(-96.8, -40.1) * mm});
            skLineSegment(sketch, "E22.146.1", {"start": v(-95.67, -38.65) * mm, "end": v(-97.48, -38.4) * mm});
            skLineSegment(sketch, "E22.147.0", {"start": v(-94.27, -41.97) * mm, "end": v(-95.34, -43.45) * mm});
            skLineSegment(sketch, "E22.147.1", {"start": v(-94.27, -41.97) * mm, "end": v(-96.08, -41.78) * mm});
            skLineSegment(sketch, "E22.148.0", {"start": v(-92.74, -45.23) * mm, "end": v(-93.77, -46.75) * mm});
            skLineSegment(sketch, "E22.148.1", {"start": v(-92.74, -45.23) * mm, "end": v(-94.57, -45.1) * mm});
            skLineSegment(sketch, "E22.149.0", {"start": v(-91.1, -48.44) * mm, "end": v(-92.08, -50) * mm});
            skLineSegment(sketch, "E22.149.1", {"start": v(-91.1, -48.44) * mm, "end": v(-92.94, -48.38) * mm});
            skLineSegment(sketch, "E22.150.0", {"start": v(-89.36, -51.6) * mm, "end": v(-90.28, -53.18) * mm});
            skLineSegment(sketch, "E22.150.1", {"start": v(-89.36, -51.6) * mm, "end": v(-91.2, -51.6) * mm});
            skLineSegment(sketch, "E22.151.0", {"start": v(-87.5, -54.68) * mm, "end": v(-88.37, -56.3) * mm});
            skLineSegment(sketch, "E22.151.1", {"start": v(-87.5, -54.68) * mm, "end": v(-89.34, -54.74) * mm});
            skLineSegment(sketch, "E22.152.0", {"start": v(-85.55, -57.7) * mm, "end": v(-86.35, -59.35) * mm});
            skLineSegment(sketch, "E22.152.1", {"start": v(-85.55, -57.7) * mm, "end": v(-87.37, -57.83) * mm});
            skLineSegment(sketch, "E22.153.0", {"start": v(-83.48, -60.65) * mm, "end": v(-84.22, -62.32) * mm});
            skLineSegment(sketch, "E22.153.1", {"start": v(-83.48, -60.65) * mm, "end": v(-85.3, -60.84) * mm});
            skLineSegment(sketch, "E22.154.0", {"start": v(-81.31, -63.53) * mm, "end": v(-82, -65.22) * mm});
            skLineSegment(sketch, "E22.154.1", {"start": v(-81.31, -63.53) * mm, "end": v(-83.12, -63.78) * mm});
            skLineSegment(sketch, "E22.155.0", {"start": v(-79.05, -66.33) * mm, "end": v(-79.67, -68.05) * mm});
            skLineSegment(sketch, "E22.155.1", {"start": v(-79.05, -66.33) * mm, "end": v(-80.85, -66.65) * mm});
            skLineSegment(sketch, "E22.156.0", {"start": v(-76.68, -69.05) * mm, "end": v(-77.25, -70.78) * mm});
            skLineSegment(sketch, "E22.156.1", {"start": v(-76.68, -69.05) * mm, "end": v(-78.47, -69.43) * mm});
            skLineSegment(sketch, "E22.157.0", {"start": v(-74.23, -71.68) * mm, "end": v(-74.73, -73.44) * mm});
            skLineSegment(sketch, "E22.157.1", {"start": v(-74.23, -71.68) * mm, "end": v(-76, -72.12) * mm});
            skLineSegment(sketch, "E22.158.0", {"start": v(-71.68, -74.23) * mm, "end": v(-72.12, -76) * mm});
            skLineSegment(sketch, "E22.158.1", {"start": v(-71.68, -74.23) * mm, "end": v(-73.44, -74.73) * mm});
            skLineSegment(sketch, "E22.159.0", {"start": v(-69.05, -76.68) * mm, "end": v(-69.43, -78.47) * mm});
            skLineSegment(sketch, "E22.159.1", {"start": v(-69.05, -76.68) * mm, "end": v(-70.78, -77.25) * mm});
            skLineSegment(sketch, "E22.160.0", {"start": v(-66.33, -79.05) * mm, "end": v(-66.65, -80.85) * mm});
            skLineSegment(sketch, "E22.160.1", {"start": v(-66.33, -79.05) * mm, "end": v(-68.05, -79.67) * mm});
            skLineSegment(sketch, "E22.161.0", {"start": v(-63.53, -81.31) * mm, "end": v(-63.78, -83.12) * mm});
            skLineSegment(sketch, "E22.161.1", {"start": v(-63.53, -81.31) * mm, "end": v(-65.22, -82) * mm});
            skLineSegment(sketch, "E22.162.0", {"start": v(-60.65, -83.48) * mm, "end": v(-60.84, -85.3) * mm});
            skLineSegment(sketch, "E22.162.1", {"start": v(-60.65, -83.48) * mm, "end": v(-62.32, -84.22) * mm});
            skLineSegment(sketch, "E22.163.0", {"start": v(-57.7, -85.55) * mm, "end": v(-57.83, -87.37) * mm});
            skLineSegment(sketch, "E22.163.1", {"start": v(-57.7, -85.55) * mm, "end": v(-59.35, -86.35) * mm});
            skLineSegment(sketch, "E22.164.0", {"start": v(-54.68, -87.5) * mm, "end": v(-54.74, -89.34) * mm});
            skLineSegment(sketch, "E22.164.1", {"start": v(-54.68, -87.5) * mm, "end": v(-56.3, -88.37) * mm});
            skLineSegment(sketch, "E22.165.0", {"start": v(-51.6, -89.36) * mm, "end": v(-51.6, -91.2) * mm});
            skLineSegment(sketch, "E22.165.1", {"start": v(-51.6, -89.36) * mm, "end": v(-53.18, -90.28) * mm});
            skLineSegment(sketch, "E22.166.0", {"start": v(-48.44, -91.1) * mm, "end": v(-48.38, -92.94) * mm});
            skLineSegment(sketch, "E22.166.1", {"start": v(-48.44, -91.1) * mm, "end": v(-50, -92.08) * mm});
            skLineSegment(sketch, "E22.167.0", {"start": v(-45.23, -92.74) * mm, "end": v(-45.1, -94.57) * mm});
            skLineSegment(sketch, "E22.167.1", {"start": v(-45.23, -92.74) * mm, "end": v(-46.75, -93.77) * mm});
            skLineSegment(sketch, "E22.168.0", {"start": v(-41.97, -94.27) * mm, "end": v(-41.78, -96.08) * mm});
            skLineSegment(sketch, "E22.168.1", {"start": v(-41.97, -94.27) * mm, "end": v(-43.45, -95.34) * mm});
            skLineSegment(sketch, "E22.169.0", {"start": v(-38.65, -95.67) * mm, "end": v(-38.4, -97.48) * mm});
            skLineSegment(sketch, "E22.169.1", {"start": v(-38.65, -95.67) * mm, "end": v(-40.1, -96.8) * mm});
            skLineSegment(sketch, "E22.170.0", {"start": v(-35.3, -96.96) * mm, "end": v(-34.97, -98.77) * mm});
            skLineSegment(sketch, "E22.170.1", {"start": v(-35.3, -96.96) * mm, "end": v(-36.7, -98.14) * mm});
            skLineSegment(sketch, "E22.171.0", {"start": v(-31.89, -98.14) * mm, "end": v(-31.5, -99.93) * mm});
            skLineSegment(sketch, "E22.171.1", {"start": v(-31.89, -98.14) * mm, "end": v(-33.25, -99.36) * mm});
            skLineSegment(sketch, "E22.172.0", {"start": v(-28.44, -99.2) * mm, "end": v(-28, -100.96) * mm});
            skLineSegment(sketch, "E22.172.1", {"start": v(-28.44, -99.2) * mm, "end": v(-29.76, -100.46) * mm});
            skLineSegment(sketch, "E22.173.0", {"start": v(-24.96, -100.12) * mm, "end": v(-24.46, -101.88) * mm});
            skLineSegment(sketch, "E22.173.1", {"start": v(-24.96, -100.12) * mm, "end": v(-26.23, -101.44) * mm});
            skLineSegment(sketch, "E22.174.0", {"start": v(-21.45, -100.93) * mm, "end": v(-20.89, -102.67) * mm});
            skLineSegment(sketch, "E22.174.1", {"start": v(-21.45, -100.93) * mm, "end": v(-22.68, -102.3) * mm});
            skLineSegment(sketch, "E22.175.0", {"start": v(-17.92, -101.62) * mm, "end": v(-17.3, -103.34) * mm});
            skLineSegment(sketch, "E22.175.1", {"start": v(-17.92, -101.62) * mm, "end": v(-19.1, -103.02) * mm});
            skLineSegment(sketch, "E22.176.0", {"start": v(-14.36, -102.18) * mm, "end": v(-13.68, -103.88) * mm});
            skLineSegment(sketch, "E22.176.1", {"start": v(-14.36, -102.18) * mm, "end": v(-15.49, -103.62) * mm});
            skLineSegment(sketch, "E22.177.0", {"start": v(-10.79, -102.62) * mm, "end": v(-10.04, -104.3) * mm});
            skLineSegment(sketch, "E22.177.1", {"start": v(-10.79, -102.62) * mm, "end": v(-11.86, -104.1) * mm});
            skLineSegment(sketch, "E22.178.0", {"start": v(-7.2, -102.94) * mm, "end": v(-6.4, -104.58) * mm});
            skLineSegment(sketch, "E22.178.1", {"start": v(-7.2, -102.94) * mm, "end": v(-8.22, -104.45) * mm});
            skLineSegment(sketch, "E22.179.0", {"start": v(-3.6, -103.12) * mm, "end": v(-2.74, -104.74) * mm});
            skLineSegment(sketch, "E22.179.1", {"start": v(-3.6, -103.12) * mm, "end": v(-4.57, -104.68) * mm});
            skSolve(sketch);
        }
        {
            var Q0;
            Q0=makeQuery(id+"F2.imprint","IMPRINT",FACE,{"disambiguationData":[TD([[makeQuery(id+"F2.imprint","IMPRINT",EDGE,{"derivedFrom":sQuery(id+"F2.wireOp",EDGE,"E18")}),-1.0]])]});
            extrude(context, id + "F3", {"entities" : qUnion([Q0]), "operationType" : NewBodyOperationType.ADD, "oppositeDirection" : true, "depth" : 6.35 * mm, "offsetDistance" : 25.4 * mm});
        }
    });
